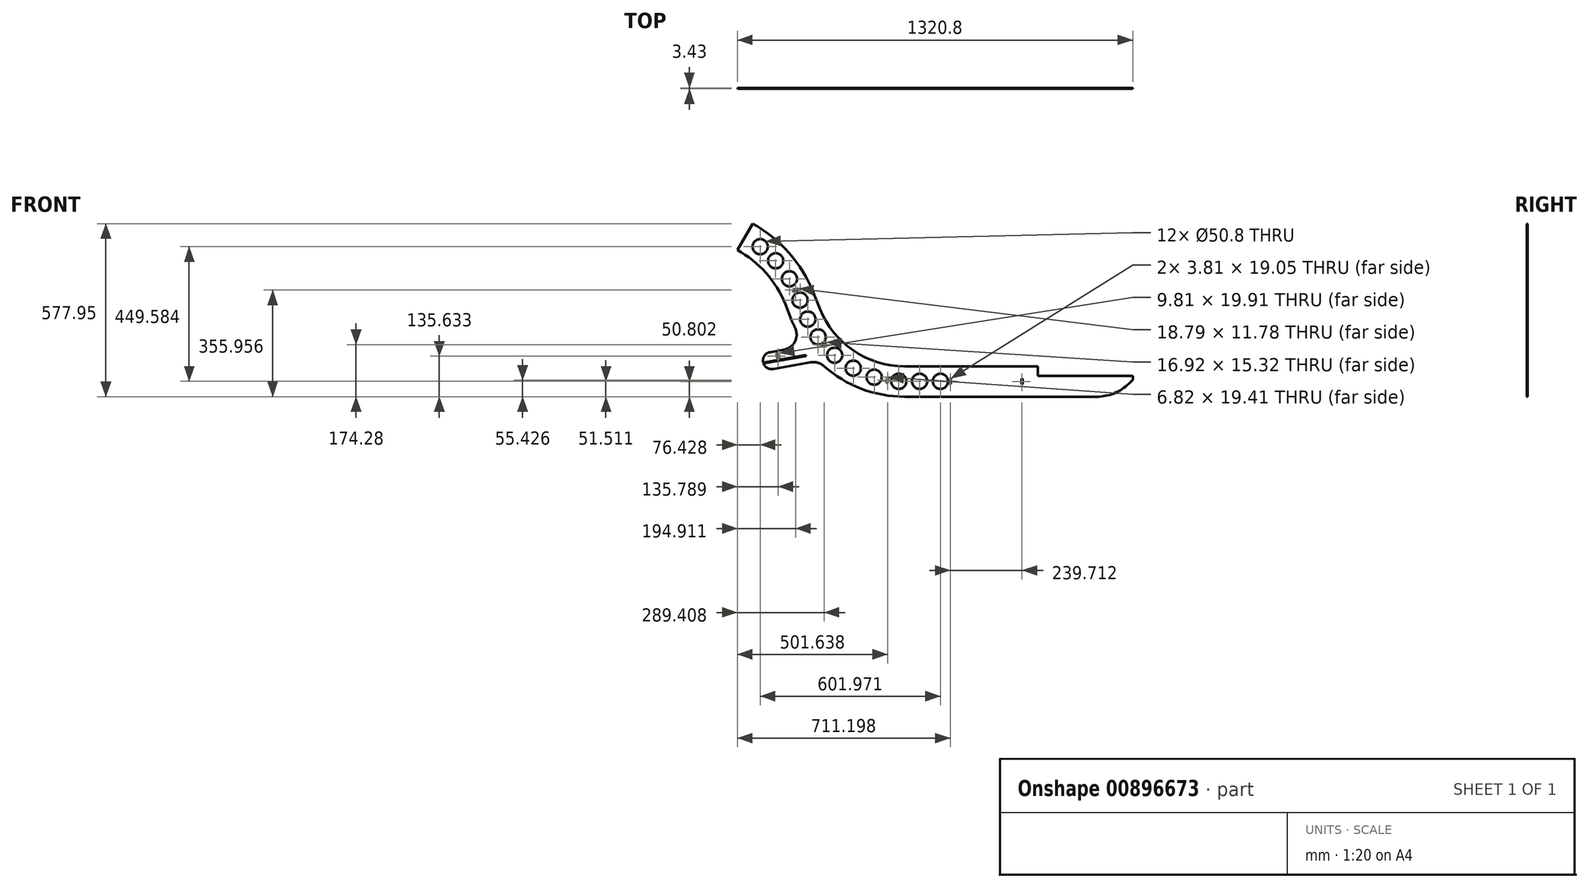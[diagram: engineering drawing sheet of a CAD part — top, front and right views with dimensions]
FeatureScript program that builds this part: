
annotation { "Feature Type Name" : "Feature", "Feature Type Description" : "" }
export const myFeature = defineFeature(function(context is Context, id is Id, definition is map)
    precondition{}
    {
        {
            var Q0;
            Q0=qCreatedBy(makeId("Front.planeOp"),FACE);
            var sketch = newSketch(context, id + "F0", { "sketchPlane" : qUnion([Q0])});
            skArc(sketch, "E0", {"start": v(-599.57, -485.26) * mm, "mid": v(-473.9, -561.54) * mm, "end": v(-329.33, -588.13) * mm});
            skArc(sketch, "E1", {"start": v(-599.57, -485.26) * mm, "mid": v(-619.48, -474.33) * mm, "end": v(-642.17, -473.18) * mm});
            skLineSegment(sketch, "E2", {"start": v(-768.87, -495.52) * mm, "end": v(-642.17, -473.18) * mm});
            skLineSegment(sketch, "E3", {"start": v(-658.51, -452.2) * mm, "end": v(-659.17, -448.45) * mm});
            skLineSegment(sketch, "E4", {"start": v(-659.17, -448.45) * mm, "end": v(-801.72, -473.58) * mm});
            skArc(sketch, "E5", {"start": v(-778.8, -439.24) * mm, "mid": v(-797.6, -451.51) * mm, "end": v(-801.72, -473.58) * mm});
            skLineSegment(sketch, "E6", {"start": v(-732.02, -430.99) * mm, "end": v(-778.8, -439.24) * mm});
            skArc(sketch, "E7", {"start": v(-732.02, -430.99) * mm, "mid": v(-695.61, -404.09) * mm, "end": v(-695.12, -358.82) * mm});
            skArc(sketch, "E8", {"start": v(-706.97, -331.9) * mm, "mid": v(-701.29, -345.47) * mm, "end": v(-695.12, -358.82) * mm});
            skLineSegment(sketch, "E9", {"start": v(-728.03, -278.93) * mm, "end": v(-706.97, -331.9) * mm});
            skArc(sketch, "E10", {"start": v(-728.03, -278.93) * mm, "mid": v(-792.27, -174.54) * mm, "end": v(-888.13, -98.16) * mm});
            skLineSegment(sketch, "E11", {"start": v(-837.33, -10.18) * mm, "end": v(-888.13, -98.16) * mm});
            skArc(sketch, "E12", {"start": v(-633.71, -241.22) * mm, "mid": v(-715.48, -108.04) * mm, "end": v(-837.33, -10.18) * mm});
            skLineSegment(sketch, "E13", {"start": v(-612.52, -294.47) * mm, "end": v(-633.71, -241.22) * mm});
            skArc(sketch, "E14", {"start": v(-612.52, -294.47) * mm, "mid": v(-500.42, -433.98) * mm, "end": v(-329.33, -486.53) * mm});
            skLineSegment(sketch, "E15", {"start": v(115.17, -486.53) * mm, "end": v(-329.33, -486.53) * mm});
            skLineSegment(sketch, "E16", {"start": v(115.17, -486.53) * mm, "end": v(115.17, -518.28) * mm});
            skLineSegment(sketch, "E17", {"start": v(115.17, -518.28) * mm, "end": v(432.67, -518.28) * mm});
            skLineSegment(sketch, "E18", {"start": v(432.67, -530.98) * mm, "end": v(432.67, -518.28) * mm});
            skLineSegment(sketch, "E19", {"start": v(420.15, -543.5) * mm, "end": v(432.67, -530.98) * mm});
            skArc(sketch, "E20", {"start": v(312.4, -588.13) * mm, "mid": v(370.71, -576.53) * mm, "end": v(420.15, -543.5) * mm});
            skLineSegment(sketch, "E21", {"start": v(-329.33, -588.13) * mm, "end": v(312.4, -588.13) * mm});
            skLineSegment(sketch, "E22", {"start": v(-757.25, -443.69) * mm, "end": v(-753.94, -462.45) * mm});
            skLineSegment(sketch, "E23", {"start": v(-753.94, -462.45) * mm, "end": v(-747.43, -461.3) * mm});
            skLineSegment(sketch, "E24", {"start": v(-747.43, -461.3) * mm, "end": v(-750.74, -442.54) * mm});
            skLineSegment(sketch, "E25", {"start": v(-750.74, -442.54) * mm, "end": v(-757.25, -443.69) * mm});
            skLineSegment(sketch, "E26", {"start": v(-700.95, -238.06) * mm, "end": v(-683.82, -229.71) * mm});
            skLineSegment(sketch, "E27", {"start": v(-683.82, -229.71) * mm, "end": v(-685.5, -226.29) * mm});
            skLineSegment(sketch, "E28", {"start": v(-685.5, -226.29) * mm, "end": v(-702.62, -234.64) * mm});
            skLineSegment(sketch, "E29", {"start": v(-702.62, -234.64) * mm, "end": v(-700.95, -238.06) * mm});
            skLineSegment(sketch, "E30", {"start": v(-604.7, -421.51) * mm, "end": v(-590.26, -409.08) * mm});
            skLineSegment(sketch, "E31", {"start": v(-590.26, -409.08) * mm, "end": v(-592.75, -406.19) * mm});
            skLineSegment(sketch, "E32", {"start": v(-592.75, -406.19) * mm, "end": v(-607.18, -418.62) * mm});
            skLineSegment(sketch, "E33", {"start": v(-607.18, -418.62) * mm, "end": v(-604.7, -421.51) * mm});
            skLineSegment(sketch, "E34", {"start": v(-386.14, -542.41) * mm, "end": v(-383.08, -523.6) * mm});
            skLineSegment(sketch, "E35", {"start": v(-383.08, -523.6) * mm, "end": v(-386.84, -523) * mm});
            skLineSegment(sketch, "E36", {"start": v(-386.84, -523) * mm, "end": v(-389.9, -541.8) * mm});
            skLineSegment(sketch, "E37", {"start": v(-389.9, -541.8) * mm, "end": v(-386.14, -542.41) * mm});
            skLineSegment(sketch, "E38", {"start": v(-175.03, -527.8) * mm, "end": v(-178.84, -527.8) * mm});
            skLineSegment(sketch, "E39", {"start": v(-178.84, -527.8) * mm, "end": v(-178.84, -546.85) * mm});
            skLineSegment(sketch, "E40", {"start": v(-178.84, -546.85) * mm, "end": v(-175.03, -546.85) * mm});
            skLineSegment(sketch, "E41", {"start": v(-175.03, -546.85) * mm, "end": v(-175.03, -527.8) * mm});
            skLineSegment(sketch, "E42", {"start": v(60.88, -546.85) * mm, "end": v(64.69, -546.85) * mm});
            skLineSegment(sketch, "E43", {"start": v(64.69, -546.85) * mm, "end": v(64.69, -527.8) * mm});
            skLineSegment(sketch, "E44", {"start": v(64.69, -527.8) * mm, "end": v(60.88, -527.8) * mm});
            skLineSegment(sketch, "E45", {"start": v(60.88, -527.8) * mm, "end": v(60.88, -546.85) * mm});
            skCircle(sketch, "E46", {"center": v(-811.7, -87.04) * mm, "radius": 25.4 * mm});
            skCircle(sketch, "E47", {"center": v(-760.12, -134.15) * mm, "radius": 25.4 * mm});
            skCircle(sketch, "E48", {"center": v(-713.86, -194.48) * mm, "radius": 25.4 * mm});
            skCircle(sketch, "E49", {"center": v(-678.73, -265.72) * mm, "radius": 25.4 * mm});
            skCircle(sketch, "E50", {"center": v(-652.74, -328.94) * mm, "radius": 25.4 * mm});
            skCircle(sketch, "E51", {"center": v(-618.38, -388.54) * mm, "radius": 25.4 * mm});
            skCircle(sketch, "E52", {"center": v(-563, -449.54) * mm, "radius": 25.4 * mm});
            skCircle(sketch, "E53", {"center": v(-500.88, -493.1) * mm, "radius": 25.4 * mm});
            skCircle(sketch, "E54", {"center": v(-431.02, -522.77) * mm, "radius": 25.4 * mm});
            skCircle(sketch, "E55", {"center": v(-349, -536.62) * mm, "radius": 25.4 * mm});
            skCircle(sketch, "E56", {"center": v(-279.4, -536.62) * mm, "radius": 25.4 * mm});
            skCircle(sketch, "E57", {"center": v(-209.73, -536.62) * mm, "radius": 25.4 * mm});
            skLineSegment(sketch, "E58", {"start": v(-800.64, -477.26) * mm, "end": v(-658.51, -452.2) * mm});
            skArc(sketch, "E59", {"start": v(-800.64, -477.26) * mm, "mid": v(-788.07, -492.15) * mm, "end": v(-768.87, -495.52) * mm});
            skSolve(sketch);
        }
        {
            var Q0;
            Q0 = qSketchRegion(id + "F0", true);
            extrude(context, id + "F1", {"entities" : qUnion([Q0]), "depth" : 3.43 * mm, "offsetDistance" : 25.4 * mm});
        }
    });
